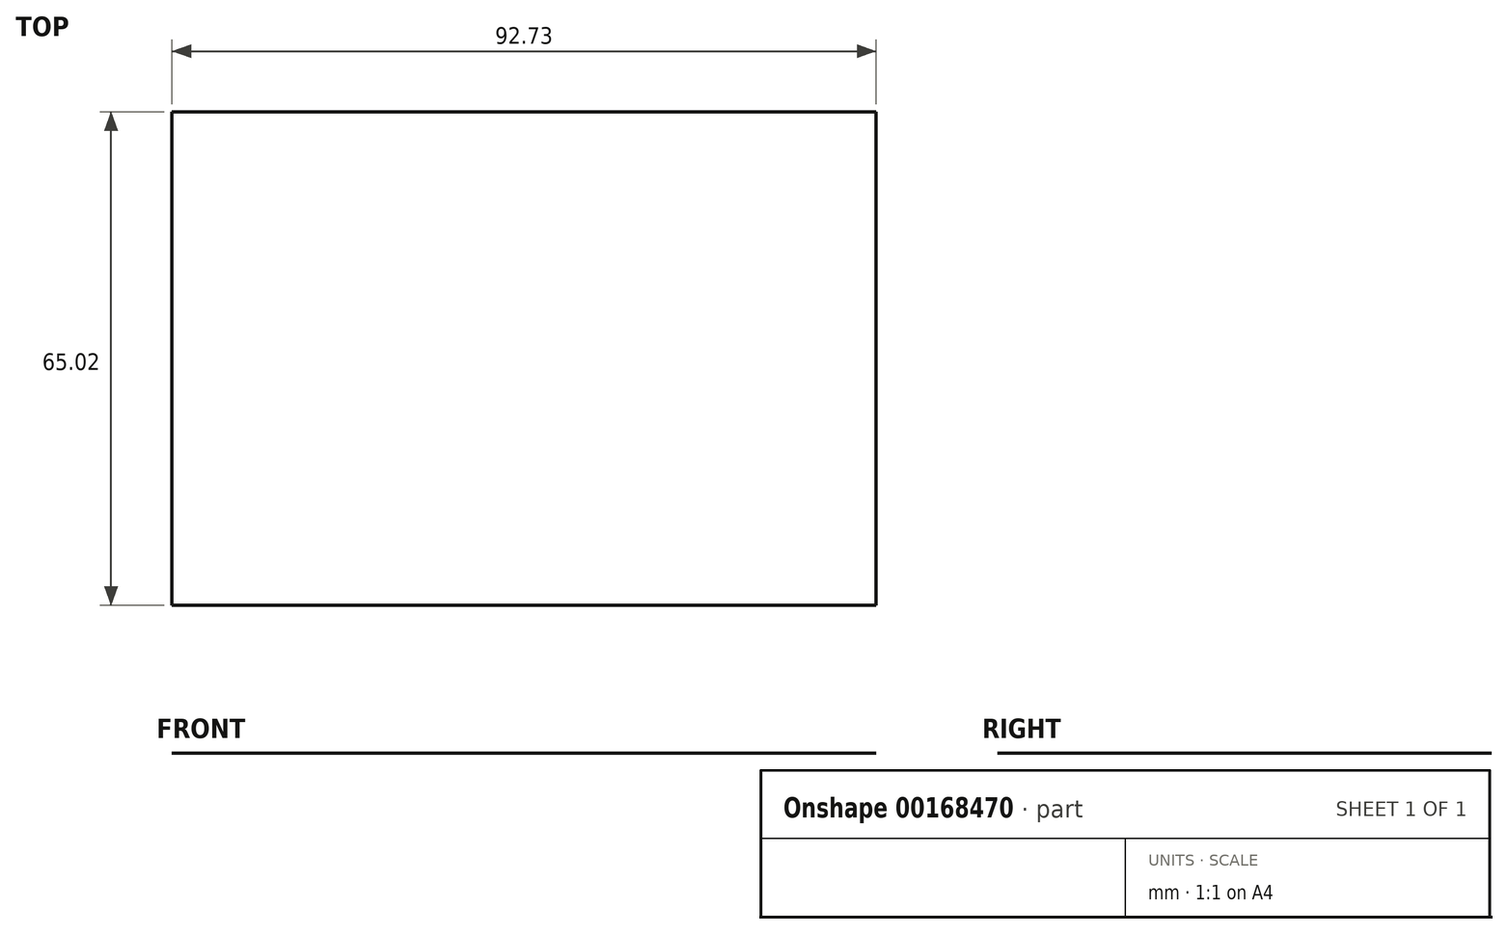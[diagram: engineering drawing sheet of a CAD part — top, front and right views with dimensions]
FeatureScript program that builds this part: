
annotation { "Feature Type Name" : "Feature", "Feature Type Description" : "" }
export const myFeature = defineFeature(function(context is Context, id is Id, definition is map)
    precondition{}
    {
        {
            var Q0;
            Q0=qCreatedBy(makeId("Front.planeOp"),FACE);
            var sketch = newSketch(context, id + "F0", { "sketchPlane" : qUnion([Q0])});
            skLineSegment(sketch, "E0", {"start": v(-92.73, 56.16) * mm, "end": v(0, 56.16) * mm});
            skSolve(sketch);
        }
        {
            var Q0;
            Q0=sQuery(id+"F0.wireOp",EDGE,"E0");
            extrude(context, id + "F1", {"bodyType" : ToolBodyType.SURFACE, "surfaceEntities" : qUnion([Q0]), "depth" : 65.02 * mm});
        }
    });
